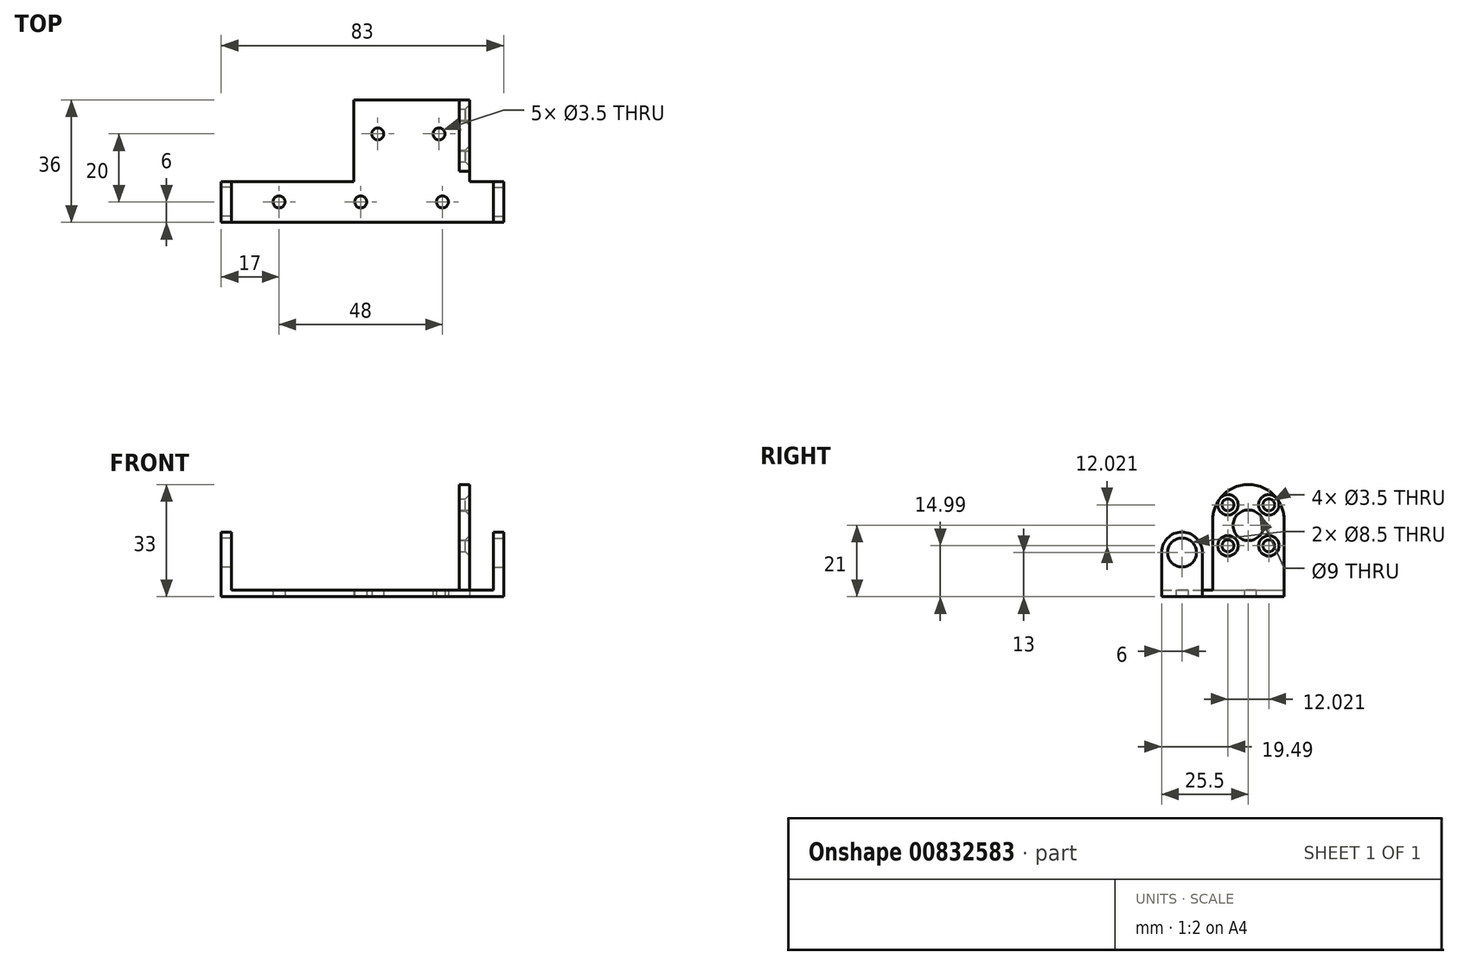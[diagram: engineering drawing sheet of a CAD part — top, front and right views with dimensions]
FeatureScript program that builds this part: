
annotation { "Feature Type Name" : "Feature", "Feature Type Description" : "" }
export const myFeature = defineFeature(function(context is Context, id is Id, definition is map)
    precondition{}
    {
        {
            var Q0;
            Q0=qCreatedBy(makeId("Top.planeOp"),FACE);
            var sketch = newSketch(context, id + "F0", { "sketchPlane" : qUnion([Q0])});
            skLineSegment(sketch, "E0.bottom", {"start": v(0, 0) * mm, "end": v(83, 0) * mm});
            skLineSegment(sketch, "E0.top", {"start": v(0, 12) * mm, "end": v(39, 12) * mm});
            skLineSegment(sketch, "E0.left", {"start": v(0, 0) * mm, "end": v(0, 12) * mm});
            skLineSegment(sketch, "E0.right", {"start": v(83, 0) * mm, "end": v(83, 12) * mm});
            skLineSegment(sketch, "E1", {"start": v(39, 12) * mm, "end": v(39, 36) * mm});
            skLineSegment(sketch, "E2", {"start": v(39, 36) * mm, "end": v(73, 36) * mm});
            skLineSegment(sketch, "E3", {"start": v(73, 36) * mm, "end": v(73, 12) * mm});
            skLineSegment(sketch, "E4.trimOffspring", {"start": v(73, 12) * mm, "end": v(83, 12) * mm});
            skCircle(sketch, "E5", {"center": v(17, 6) * mm, "radius": 1.75 * mm});
            skCircle(sketch, "E6", {"center": v(41, 6) * mm, "radius": 1.75 * mm});
            skPoint(sketch, "E6.centerSnap0", {"position": v(0, 6) * mm});
            skCircle(sketch, "E7", {"center": v(65, 6) * mm, "radius": 1.75 * mm});
            skCircle(sketch, "E8", {"center": v(46, 26) * mm, "radius": 1.75 * mm});
            skCircle(sketch, "E9", {"center": v(64, 26) * mm, "radius": 1.75 * mm});
            skSolve(sketch);
        }
        {
            var Q0;
            Q0 = qSketchRegion(id + "F0", true);
            extrude(context, id + "F1", {"entities" : qUnion([Q0]), "depth" : 2 * mm, "offsetDistance" : 25 * mm});
        }
        {
            var Q0;
            Q0=qCreatedBy(makeId("Right.planeOp"),FACE);
            cPlane(context, id + "F2", {"entities" : qUnion([Q0]), "cplaneType" : CPlaneType.OFFSET, "offset" : 83 * mm, "width" : 150 * mm, "height" : 150 * mm});
        }
        {
            var Q0;
            Q0=qCreatedBy(makeId("Right.planeOp"),FACE);
            var sketch = newSketch(context, id + "F3", { "sketchPlane" : qUnion([Q0])});
            skLineSegment(sketch, "E10.bottom", {"start": v(0, 0) * mm, "end": v(12, 0) * mm});
            skLineSegment(sketch, "E10.left", {"start": v(0, 0) * mm, "end": v(0, 13) * mm});
            skLineSegment(sketch, "E10.right", {"start": v(12, 0) * mm, "end": v(12, 13) * mm});
            skArc(sketch, "E11", {"start": v(12, 13) * mm, "mid": v(6, 19) * mm, "end": v(0, 13) * mm});
            skCircle(sketch, "E12", {"center": v(6, 13) * mm, "radius": 4.25 * mm});
            skSolve(sketch);
        }
        {
            var Q0;
            Q0 = qSketchRegion(id + "F3", true);
            extrude(context, id + "F4", {"entities" : qUnion([Q0]), "operationType" : NewBodyOperationType.ADD, "depth" : 3 * mm, "offsetDistance" : 25 * mm});
        }
        {
            var Q0;
            Q0=qCreatedBy(id+"F2.planeOp",FACE);
            var sketch = newSketch(context, id + "F5", { "sketchPlane" : qUnion([Q0])});
            skLineSegment(sketch, "E13.bottom", {"start": v(0, 0) * mm, "end": v(12, 0) * mm});
            skLineSegment(sketch, "E13.left", {"start": v(0, 0) * mm, "end": v(0, 13) * mm});
            skLineSegment(sketch, "E13.right", {"start": v(12, 0) * mm, "end": v(12, 13) * mm});
            skArc(sketch, "E14", {"start": v(12, 13) * mm, "mid": v(6, 19) * mm, "end": v(0, 13) * mm});
            skCircle(sketch, "E15", {"center": v(6, 13) * mm, "radius": 4.25 * mm});
            skSolve(sketch);
        }
        {
            var Q0;
            Q0 = qSketchRegion(id + "F5", true);
            extrude(context, id + "F6", {"entities" : qUnion([Q0]), "operationType" : NewBodyOperationType.ADD, "oppositeDirection" : true, "depth" : 3 * mm, "offsetDistance" : 25 * mm});
        }
        {
            var Q0;
            Q0=qCreatedBy(id+"F2.planeOp",FACE);
            cPlane(context, id + "F7", {"entities" : qUnion([Q0]), "cplaneType" : CPlaneType.OFFSET, "offset" : 10 * mm, "oppositeDirection" : true, "width" : 150 * mm, "height" : 150 * mm});
        }
        {
            var Q0;
            Q0=qCreatedBy(id+"F7.planeOp",FACE);
            var sketch = newSketch(context, id + "F8", { "sketchPlane" : qUnion([Q0])});
            skLineSegment(sketch, "E16", {"start": v(0, 0) * mm, "end": v(15, 0) * mm});
            skLineSegment(sketch, "E17.bottom", {"start": v(15, 0) * mm, "end": v(36, 0) * mm});
            skLineSegment(sketch, "E17.top", {"start": v(15, 22.5) * mm, "end": v(36, 22.5) * mm});
            skLineSegment(sketch, "E17.left", {"start": v(15, 0) * mm, "end": v(15, 22.5) * mm});
            skLineSegment(sketch, "E17.right", {"start": v(36, 0) * mm, "end": v(36, 22.5) * mm});
            skArc(sketch, "E18", {"start": v(36, 22.5) * mm, "mid": v(25.5, 33) * mm, "end": v(15, 22.5) * mm});
            skCircle(sketch, "E19", {"center": v(25.5, 21) * mm, "radius": 4.5 * mm});
            skPoint(sketch, "E19.centerSnap0", {"position": v(25.5, 33) * mm});
            skLineSegment(sketch, "E20", {"start": v(19.49, 27.01) * mm, "end": v(25.5, 21) * mm});
            skPoint(sketch, "E21.center", {"position": v(0, 0) * mm});
            skLineSegment(sketch, "E22", {"start": v(25.5, 33) * mm, "end": v(25.5, 13.34) * mm});
            skLineSegment(sketch, "E23", {"start": v(25.5, 21) * mm, "end": v(17.36, 21) * mm});
            skPoint(sketch, "E24", {"position": v(19.49, 27.01) * mm});
            skPoint(sketch, "E25", {"position": v(31.51, 27.01) * mm});
            skPoint(sketch, "E26", {"position": v(31.51, 14.99) * mm});
            skPoint(sketch, "E27", {"position": v(19.49, 14.99) * mm});
            skSolve(sketch);
        }
        {
            var Q0;
            Q0 = qSketchRegion(id + "F8", true);
            extrude(context, id + "F9", {"entities" : qUnion([Q0]), "operationType" : NewBodyOperationType.ADD, "oppositeDirection" : true, "depth" : 3 * mm, "offsetDistance" : 25 * mm});
        }
        {
            var Q0;
            Q0=sQuery(id+"F8.wireOp",VERTEX,"E26");
            var Q1;
            Q1=sQuery(id+"F8.wireOp",VERTEX,"E27");
            var Q2;
            Q2=sQuery(id+"F8.wireOp",VERTEX,"E24");
            var Q3;
            Q3=sQuery(id+"F8.wireOp",VERTEX,"E25");
            var Q4;
            Q4=makeQuery(id+"F1.opExtrude","SWEPT_BODY",BODY,{"disambiguationData":[OSD([sQuery(id+"F0.wireOp",EDGE,"E0.bottom"),sQuery(id+"F0.wireOp",EDGE,"E0.top"),sQuery(id+"F0.wireOp",EDGE,"E0.left"),sQuery(id+"F0.wireOp",EDGE,"E0.right"),sQuery(id+"F0.wireOp",EDGE,"E1"),sQuery(id+"F0.wireOp",EDGE,"E2"),sQuery(id+"F0.wireOp",EDGE,"E3"),sQuery(id+"F0.wireOp",EDGE,"E4.trimOffspring"),sQuery(id+"F0.wireOp",EDGE,"E5"),sQuery(id+"F0.wireOp",EDGE,"E6"),sQuery(id+"F0.wireOp",EDGE,"E7")])]});
            hole(context, id + "F10", {"style" : HoleStyle.C_SINK, "endStyle" : HoleEndStyle.THROUGH, "holeDiameter" : 3.5 * mm, "cSinkDiameter" : 6 * mm, "cSinkAngle" : 90 * degree, "majorDiameter" : 5 * mm, "isTappedThrough" : true, "tappedDepth" : 12 * mm, "tapClearance" : 3, "startFromSketch" : true, "locations" : qUnion([Q0, Q1, Q2, Q3]), "scope" : qUnion([Q4])});
        }
    });
